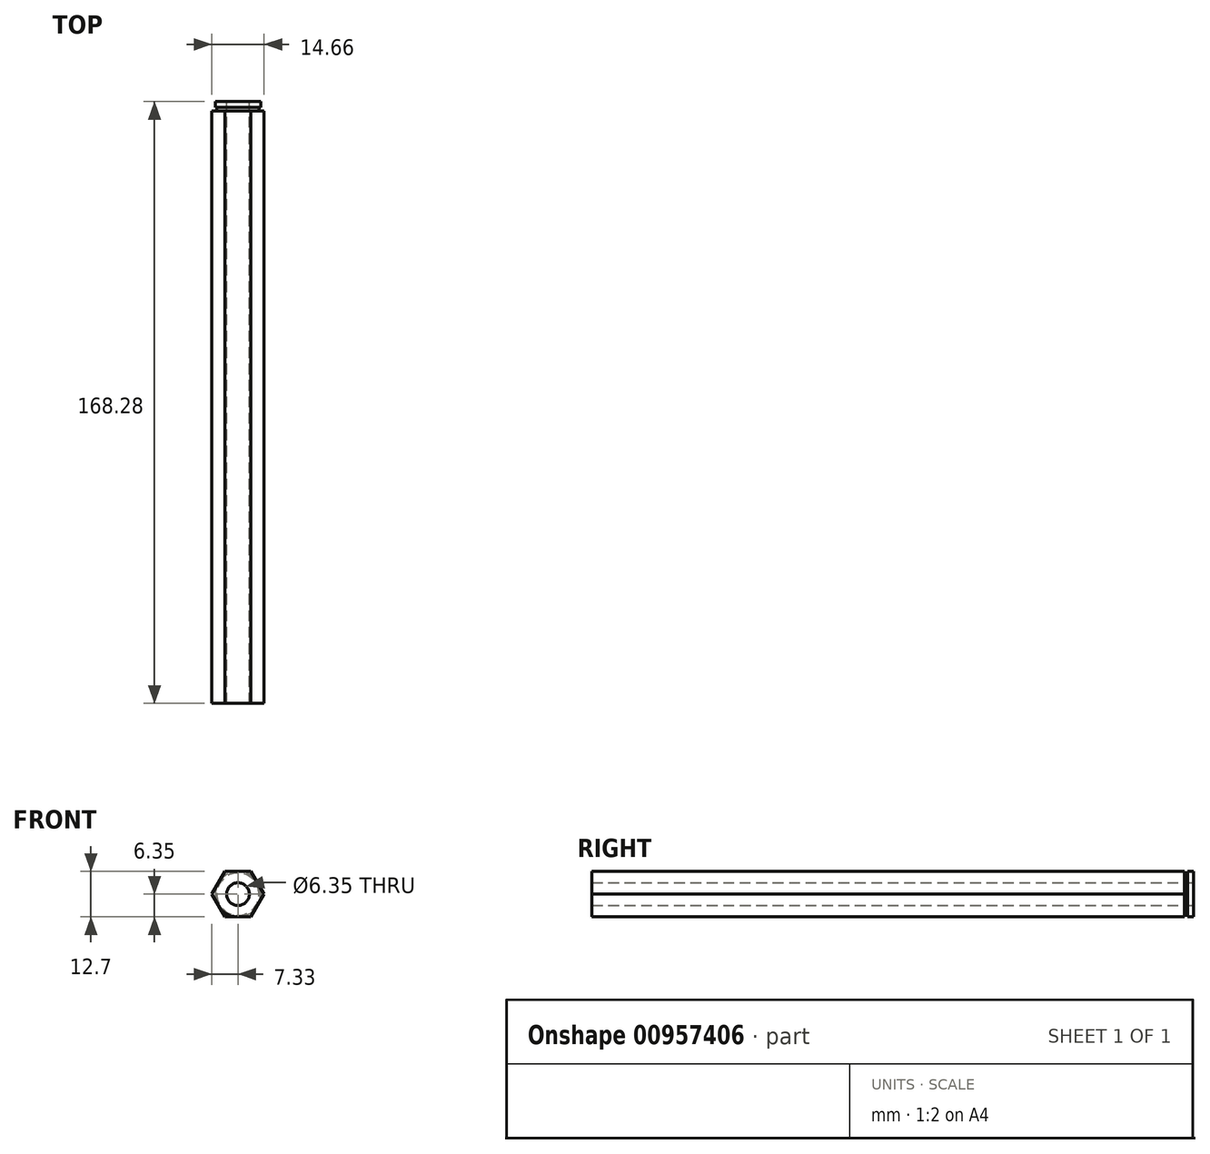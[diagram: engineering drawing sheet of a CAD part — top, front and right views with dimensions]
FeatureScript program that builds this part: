
annotation { "Feature Type Name" : "Feature", "Feature Type Description" : "" }
export const myFeature = defineFeature(function(context is Context, id is Id, definition is map)
    precondition{}
    {
        {
            var Q0;
            Q0=qCreatedBy(makeId("Front.planeOp"),FACE);
            var sketch = newSketch(context, id + "F0", { "sketchPlane" : qUnion([Q0])});
            skCircle(sketch, "E0.cCircle", {"center": v(0, 0) * mm, "radius": 6.35 * mm, "construction": true});
            skLineSegment(sketch, "E0.0", {"start": v(-3.67, 6.35) * mm, "end": v(3.67, 6.35) * mm});
            skLineSegment(sketch, "E0.1", {"start": v(3.67, 6.35) * mm, "end": v(7.33, 0) * mm});
            skLineSegment(sketch, "E0.2", {"start": v(7.33, 0) * mm, "end": v(3.67, -6.35) * mm});
            skLineSegment(sketch, "E0.3", {"start": v(3.67, -6.35) * mm, "end": v(-3.67, -6.35) * mm});
            skLineSegment(sketch, "E0.4", {"start": v(-3.67, -6.35) * mm, "end": v(-7.33, 0) * mm});
            skLineSegment(sketch, "E0.5", {"start": v(-7.33, 0) * mm, "end": v(-3.67, 6.35) * mm});
            skPoint(sketch, "E0.0.midPoint", {"position": v(0, 6.35) * mm});
            skCircle(sketch, "E1", {"center": v(0, 0) * mm, "radius": 3.18 * mm});
            skSolve(sketch);
        }
        {
            var Q0;
            Q0 = qSketchRegion(id + "F0", true);
            extrude(context, id + "F1", {"entities" : qUnion([Q0]), "depth" : 168.27 * mm, "offsetDistance" : 25.4 * mm});
        }
        {
            var Q0;
            Q0=qCreatedBy(makeId("Top.planeOp"),FACE);
            var sketch = newSketch(context, id + "F2", { "sketchPlane" : qUnion([Q0])});
            skLineSegment(sketch, "E2", {"start": v(-6.35, 0) * mm, "end": v(-6.35, -1.59) * mm});
            skLineSegment(sketch, "E3", {"start": v(-6.35, -1.59) * mm, "end": v(-5.94, -1.59) * mm});
            skLineSegment(sketch, "E4", {"start": v(-5.94, -1.59) * mm, "end": v(-5.94, -2.58) * mm});
            skLineSegment(sketch, "E5", {"start": v(-5.94, -2.58) * mm, "end": v(-7.33, -2.58) * mm});
            skLineSegment(sketch, "E6", {"start": v(-7.33, -2.58) * mm, "end": v(-7.33, 0) * mm});
            skLineSegment(sketch, "E7", {"start": v(-7.33, 0) * mm, "end": v(-6.35, 0) * mm});
            skLineSegment(sketch, "E8", {"start": v(0, 0) * mm, "end": v(0, -2.58) * mm, "construction": true});
            skSolve(sketch);
        }
        {
            var Q0;
            Q0 = qSketchRegion(id + "F2", true);
            var Q1;
            Q1=sQuery(id+"F2.wireOp",EDGE,"E8");
            revolve(context, id + "F3", {"operationType" : NewBodyOperationType.REMOVE, "surfaceOperationType" : NewSurfaceOperationType.NEW, "entities" : qUnion([Q0]), "axis" : qUnion([Q1]), "revolveType" : RevolveType.FULL, "oppositeDirection" : true});
        }
    });
